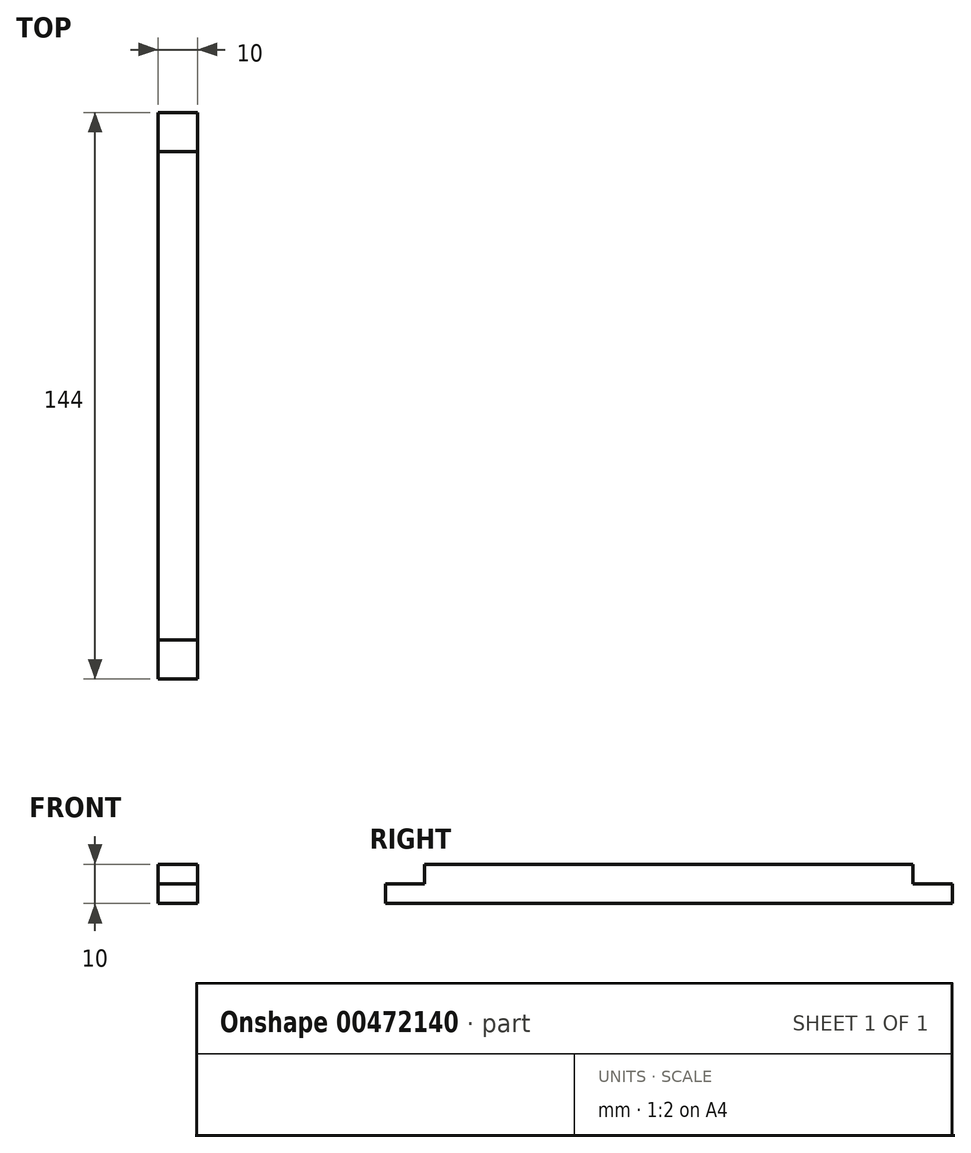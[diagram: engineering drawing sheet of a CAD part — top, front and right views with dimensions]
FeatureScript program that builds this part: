
annotation { "Feature Type Name" : "Feature", "Feature Type Description" : "" }
export const myFeature = defineFeature(function(context is Context, id is Id, definition is map)
    precondition{}
    {
        {
            var Q0;
            Q0=qCreatedBy(makeId("Front.planeOp"),FACE);
            var sketch = newSketch(context, id + "F0", { "sketchPlane" : qUnion([Q0])});
            skLineSegment(sketch, "E0.bottom", {"start": v(5, -5) * mm, "end": v(-5, -5) * mm});
            skLineSegment(sketch, "E0.top", {"start": v(5, 5) * mm, "end": v(-5, 5) * mm});
            skLineSegment(sketch, "E0.left", {"start": v(5, -5) * mm, "end": v(5, 5) * mm});
            skLineSegment(sketch, "E0.right", {"start": v(-5, -5) * mm, "end": v(-5, 5) * mm});
            skPoint(sketch, "E0.middle", {"position": v(0, 0) * mm});
            skSolve(sketch);
        }
        {
            var Q0;
            Q0=makeQuery(id+"F0.imprint","IMPRINT",FACE,{"disambiguationData":[TD([[makeQuery(id+"F0.imprint","IMPRINT",EDGE,{"derivedFrom":sQuery(id+"F0.wireOp",EDGE,"E0.bottom")}),-1.0]])]});
            extrude(context, id + "F1", {"entities" : qUnion([Q0]), "depth" : 144 * mm});
        }
        {
            var Q0;
            Q0=makeQuery(id+"F1.opExtrude","SWEPT_FACE",FACE,{"disambiguationData":[OSD([sQuery(id+"F0.wireOp",EDGE,"E0.left")])]});
            var sketch = newSketch(context, id + "F2", { "sketchPlane" : qUnion([Q0])});
            skLineSegment(sketch, "E1", {"start": v(-134, 5) * mm, "end": v(-134, 0) * mm});
            skLineSegment(sketch, "E2", {"start": v(-134, 0) * mm, "end": v(-144, 0) * mm});
            skLineSegment(sketch, "E3", {"start": v(-10, 5) * mm, "end": v(-10, 0) * mm});
            skLineSegment(sketch, "E4", {"start": v(-10, 0) * mm, "end": v(0, 0) * mm});
            skSolve(sketch);
        }
        {
            var Q0;
            {var subQ0=sQuery(id+"F2.wireOp",EDGE,"E1");Q0=makeQuery(id+"F2.imprint","IMPRINT",FACE,{"disambiguationData":[TD([[makeQuery(id+"F2.imprint","IMPRINT",EDGE,{"derivedFrom":subQ0}),-1.0]])]});}
            var Q1;
            {var subQ0=sQuery(id+"F2.wireOp",EDGE,"E3");Q1=makeQuery(id+"F2.imprint","IMPRINT",FACE,{"disambiguationData":[TD([[makeQuery(id+"F2.imprint","IMPRINT",EDGE,{"derivedFrom":subQ0}),1.0]])]});}
            extrude(context, id + "F3", {"entities" : qUnion([Q0, Q1]), "operationType" : NewBodyOperationType.REMOVE, "oppositeDirection" : true, "depth" : 10 * mm});
        }
    });
